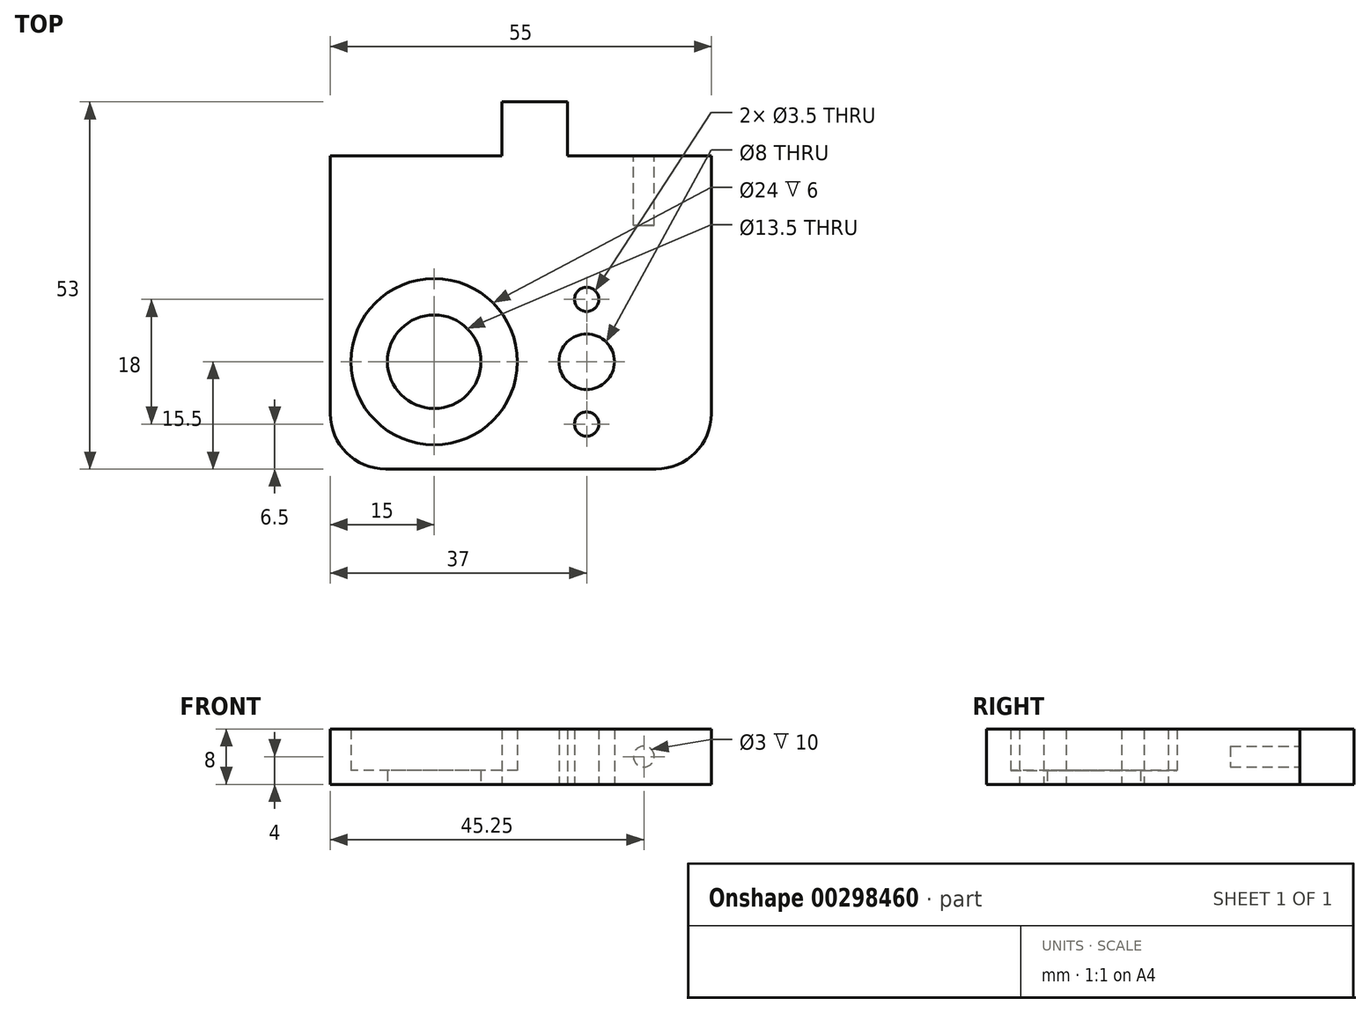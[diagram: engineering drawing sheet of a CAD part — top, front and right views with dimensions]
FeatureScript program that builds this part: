
annotation { "Feature Type Name" : "Feature", "Feature Type Description" : "" }
export const myFeature = defineFeature(function(context is Context, id is Id, definition is map)
    precondition{}
    {
        {
            var Q0;
            Q0=qCreatedBy(makeId("Top.planeOp"),FACE);
            var sketch = newSketch(context, id + "F0", { "sketchPlane" : qUnion([Q0])});
            skLineSegment(sketch, "E0.bottom", {"start": v(20.75, 0) * mm, "end": v(30.25, 0) * mm});
            skLineSegment(sketch, "E0.top", {"start": v(0, -53) * mm, "end": v(51, -53) * mm});
            skLineSegment(sketch, "E0.left", {"start": v(0, -7.8) * mm, "end": v(0, -53) * mm, "construction": true});
            skLineSegment(sketch, "E0.right", {"start": v(51, -7.8) * mm, "end": v(51, -53) * mm});
            skPoint(sketch, "E1", {"position": v(25.5, 0) * mm});
            skLineSegment(sketch, "E2.top", {"start": v(20.75, -7.8) * mm, "end": v(30.25, -7.8) * mm, "construction": true});
            skLineSegment(sketch, "E2.left", {"start": v(20.75, 0) * mm, "end": v(20.75, -7.8) * mm});
            skLineSegment(sketch, "E2.right", {"start": v(30.25, 0) * mm, "end": v(30.25, -7.8) * mm});
            skLineSegment(sketch, "E3", {"start": v(20.75, -7.8) * mm, "end": v(0, -7.8) * mm});
            skLineSegment(sketch, "E4", {"start": v(30.25, -7.8) * mm, "end": v(51, -7.8) * mm});
            skPoint(sketch, "E5.orphan", {"position": v(0, 0) * mm});
            skPoint(sketch, "E6.orphan", {"position": v(51, 0) * mm});
            skCircle(sketch, "E7", {"center": v(11, -37.5) * mm, "radius": 6.75 * mm});
            skCircle(sketch, "E8", {"center": v(33, -37.5) * mm, "radius": 4 * mm});
            skPoint(sketch, "E9.visualSharp", {"position": v(51, -53) * mm});
            skPoint(sketch, "E10.visualSharp", {"position": v(0, -53) * mm});
            skCircle(sketch, "E11", {"center": v(33, -28.5) * mm, "radius": 1.75 * mm});
            skCircle(sketch, "E12", {"center": v(33, -46.5) * mm, "radius": 1.75 * mm});
            skLineSegment(sketch, "E13", {"start": v(33, -28.5) * mm, "end": v(33, -46.5) * mm, "construction": true});
            skCircle(sketch, "E14", {"center": v(11, -37.5) * mm, "radius": 12 * mm});
            skLineSegment(sketch, "E15", {"start": v(0, -7.8) * mm, "end": v(-4, -7.8) * mm});
            skLineSegment(sketch, "E16", {"start": v(-4, -7.8) * mm, "end": v(-4, -53) * mm});
            skLineSegment(sketch, "E17", {"start": v(-4, -53) * mm, "end": v(0, -53) * mm});
            skSolve(sketch);
        }
        {
            var Q0;
            Q0=makeQuery(id+"F0.imprint","IMPRINT",FACE,{"disambiguationData":[TD([[makeQuery(id+"F0.imprint","IMPRINT",EDGE,{"derivedFrom":sQuery(id+"F0.wireOp",EDGE,"E0.top")}),1.0]])]});
            extrude(context, id + "F1", {"entities" : qUnion([Q0]), "depth" : 8 * mm});
        }
        {
            var Q0;
            Q0=makeQuery(id+"F0.imprint","IMPRINT",FACE,{"disambiguationData":[TD([[makeQuery(id+"F0.imprint","IMPRINT",EDGE,{"derivedFrom":sQuery(id+"F0.wireOp",EDGE,"E7")}),-1.0]])]});
            extrude(context, id + "F2", {"entities" : qUnion([Q0]), "operationType" : NewBodyOperationType.ADD, "depth" : 2 * mm});
        }
        {
            var Q0;
            Q0=makeQuery(id+"F1.opExtrude","SWEPT_EDGE",EDGE,{"disambiguationData":[OSD([sQuery(id+"F0.wireOp",EDGE,"E16"),sQuery(id+"F0.wireOp",EDGE,"E17")])]});
            var Q1;
            Q1=makeQuery(id+"F1.opExtrude","SWEPT_EDGE",EDGE,{"disambiguationData":[OSD([sQuery(id+"F0.wireOp",EDGE,"E0.top"),sQuery(id+"F0.wireOp",EDGE,"E0.right")])]});
            fillet(context, id + "F3", {"entities" : qUnion([Q0, Q1]), "radius" : 8 * mm, "tangentPropagation" : true, "allowEdgeOverflow" : false});
        }
        {
            var Q0;
            Q0=makeQuery(id+"F1.opExtrude","SWEPT_FACE",FACE,{"disambiguationData":[OSD([sQuery(id+"F0.wireOp",EDGE,"E4")])]});
            var sketch = newSketch(context, id + "F4", { "sketchPlane" : qUnion([Q0])});
            skLineSegment(sketch, "E18", {"start": v(-39.75, 8) * mm, "end": v(-39.75, 0) * mm, "construction": true});
            skCircle(sketch, "E19", {"center": v(-41.25, 4) * mm, "radius": 1.5 * mm});
            skPoint(sketch, "E19.centerSnap0", {"position": v(-51, 4) * mm});
            skLineSegment(sketch, "E20.bottom", {"start": v(-51, 8) * mm, "end": v(0, 8) * mm, "construction": true});
            skLineSegment(sketch, "E20.top", {"start": v(-51, 0) * mm, "end": v(0, 0) * mm, "construction": true});
            skLineSegment(sketch, "E20.left", {"start": v(-51, 8) * mm, "end": v(-51, 0) * mm, "construction": true});
            skLineSegment(sketch, "E20.right", {"start": v(0, 8) * mm, "end": v(0, 0) * mm, "construction": true});
            skLineSegment(sketch, "E21", {"start": v(-25.5, 0) * mm, "end": v(-25.5, 8) * mm, "construction": true});
            skCircle(sketch, "E22.MirrorC", {"center": v(-9.75, 4) * mm, "radius": 1.5 * mm});
            skSolve(sketch);
        }
        {
            var Q0;
            Q0=makeQuery(id+"F4.imprint","IMPRINT",FACE,{"disambiguationData":[TD([[makeQuery(id+"F4.imprint","IMPRINT",EDGE,{"derivedFrom":sQuery(id+"F4.wireOp",EDGE,"E19")}),1.0]])]});
            var Q1;
            Q1=makeQuery(id+"F4.imprint","IMPRINT",FACE,{"disambiguationData":[TD([[makeQuery(id+"F4.imprint","IMPRINT",EDGE,{"derivedFrom":sQuery(id+"F4.wireOp",EDGE,"E22.MirrorC")}),-1.0]])]});
            extrude(context, id + "F5", {"entities" : qUnion([Q0, Q1]), "operationType" : NewBodyOperationType.REMOVE, "oppositeDirection" : true, "depth" : 10 * mm});
        }
    });
